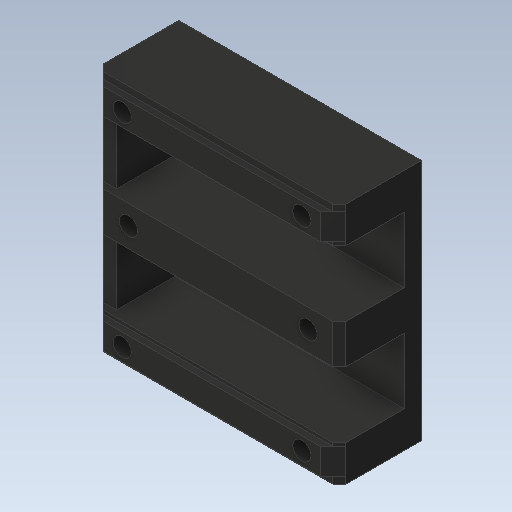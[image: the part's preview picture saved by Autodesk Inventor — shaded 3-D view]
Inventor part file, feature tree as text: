
AUTODESK INVENTOR PART (.ipt)
format: ipt  version: 2020 (Build 240168000, 168)  size: 206,336 bytes
history: native  units: mm
features: extrude x5, sketch x5, chamfer x3, other x2, pattern_linear x1
ambient origin geometry x8: Origin, YZ Plane, XZ Plane, XY Plane, X Axis, Y Axis, Z Axis, Center Point
bodies: Body1 (feature_tree)
feature tree (16):
  other  "Bryła1"
  extrude  "Wyciągnięcie proste1"  Depth=74.0mm
  extrude  "Wyciągnięcie proste2"  Depth=74.0mm
  extrude  "Wyciągnięcie proste3"  Depth=25.0mm TaperAngle=0.0deg
  other  "Płaszczyzna konstrukcyjna1"
  extrude  "Wyciągnięcie proste5"  Depth=20.0mm
  pattern_linear  "Szyk prostokątny1"  Count1=2  [1 undecoded]
  chamfer  "Faza1"  Distance=11.0mm
  chamfer  "Faza2"  Distance=11.0mm
  chamfer  "Faza3"  Distance=19.8mm
  extrude  "Wyciągnięcie proste6"  Depth=2.05mm
  sketch  "Szkic1"
  sketch  "Szkic2"
  sketch  "Szkic3"
  sketch  "Szkic5"
  sketch  "Szkic6"
note: 1 required parameter value undecoded (feature->parameter linkage not recoverable at this tier; creation-order binding heuristic only, values carry confidence <= 0.55)
